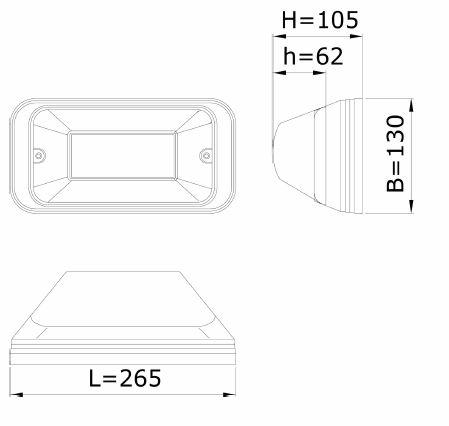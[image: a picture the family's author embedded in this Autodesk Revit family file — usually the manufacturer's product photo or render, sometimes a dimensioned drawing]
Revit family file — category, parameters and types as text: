
# Revit family: Lightronics_LightingFixture_WallAndCeiling_TPS1
name_source: partatom
category: Lighting Fixtures
revit_build: Autodesk Revit 2016 (Build: 20160314_0715(x64)
units: mm (PartAtom-declared; Revit-internal decimal feet)

## family parameters
Cut with Voids When Loaded = No
Host = Face
Light Source = Yes
OmniClass Number = 23.80.70.00
OmniClass Title = Lighting
Part Type = Normal
Room Calculation Point = No
Round Connector Dimension = Use Diameter
Shared = No

## types (1)
- TPS
    Apparent Load = 0 VA
    Assembly Code = D5020200
    AssetType = Fixed
    BIMObjectName = Lightronics_LightingFixture_WallAndCeiling_TPS
    ClassificationName = Uniclass 2015
    ClassificationValue = Pr_70_70_48_85
    Color = Housing: impactproof, flame-retardent, UV-stabilised polycarbonate in white RAL 9010, black RAL 9005 or anthracite RAL7016. Cover: polycarbonate lens, clear prismatic, opal or frosted
    Color Filter = 16777215
    Default Elevation = 1219 mm
    Depth = 130 mm  [stored 0.426509 ft]
    Description = The TPS trapezoidal surface-mounted luminaire with high light output in a contemporary design. The assembly- and maintenance-friendly TPS luminaire uses the same basic unit as the TPK and the WVK. allowing their spare parts to be seamlessly interchangeable. The TPS is suitable for both continuous and emergency lighting. The impactproof, flame-retardant cover provides safety and vandal-resistance.
    Dimming Lamp Color Temperature Shift = <None>
    DocumentationLiterature = https://specifi.bimstore.co.uk
    DurationUnit = 20 Years
    Emit from Line Length = 200 mm  [stored 0.656168 ft]
    ExpectedLife = 10
    Height = 105 mm  [stored 0.344488 ft]
    IfcExportAs = IfcLightFixtureTypeEnum.POINTSOURCE
    IfcExportType = IfcLightFixture
    Keynote = V90/510
    Length = 265 mm  [stored 0.869423 ft]
    Manufacturer = Lightronics
    ManufacturerName = Lightronics
    Material = Impact proof, flame-retardant, UV-stabilised polycarbonate
    Model = TPS
    ModelNumber = TPS
    ModelReference = IP 65
    NBSDescription = Surface luminaires
    NBSObjectName = Lightronics -  General purpose luminaires
    NBSReference = 90-60-50/405
    NominalDepth = 130 mm  [stored 0.426509 ft]
    NominalHeight = 105 mm  [stored 0.344488 ft]
    NominalLength = 265 mm  [stored 0.869423 ft]
    NumberOfPoles = 1
    Photometric Web File = TPS-MP4-16-3-180-D-F-280-230-X-W.ies
    ProductionYear = 2018
    Shape = Rectangular
    Size = 130x105x265
    Tilt Angle = 90.00°
    Type Comments = Wall and ceiling lighting – Impactproof. Surface-mounted luminaire with a contemporary design
    TypeName = TPS
    URL = https://www.lightronics.nl
    Voltage = 230 V
    WarrantyDurationParts = 5
    WarrantyDurationUnit = Years
    _BSBibleVersion = 15
    _BimSpecGuid = 0
    _CurrentRevision = 1
    _DistributedBy = www.bimstore.co.uk

note: [stored X ft] marks values corroborated as IEEE doubles in the binary element streams (Revit-internal decimal feet)

## geometry (parser evidence)
native form markers: Sweep x4
no freeform markers — native parametric forms only
